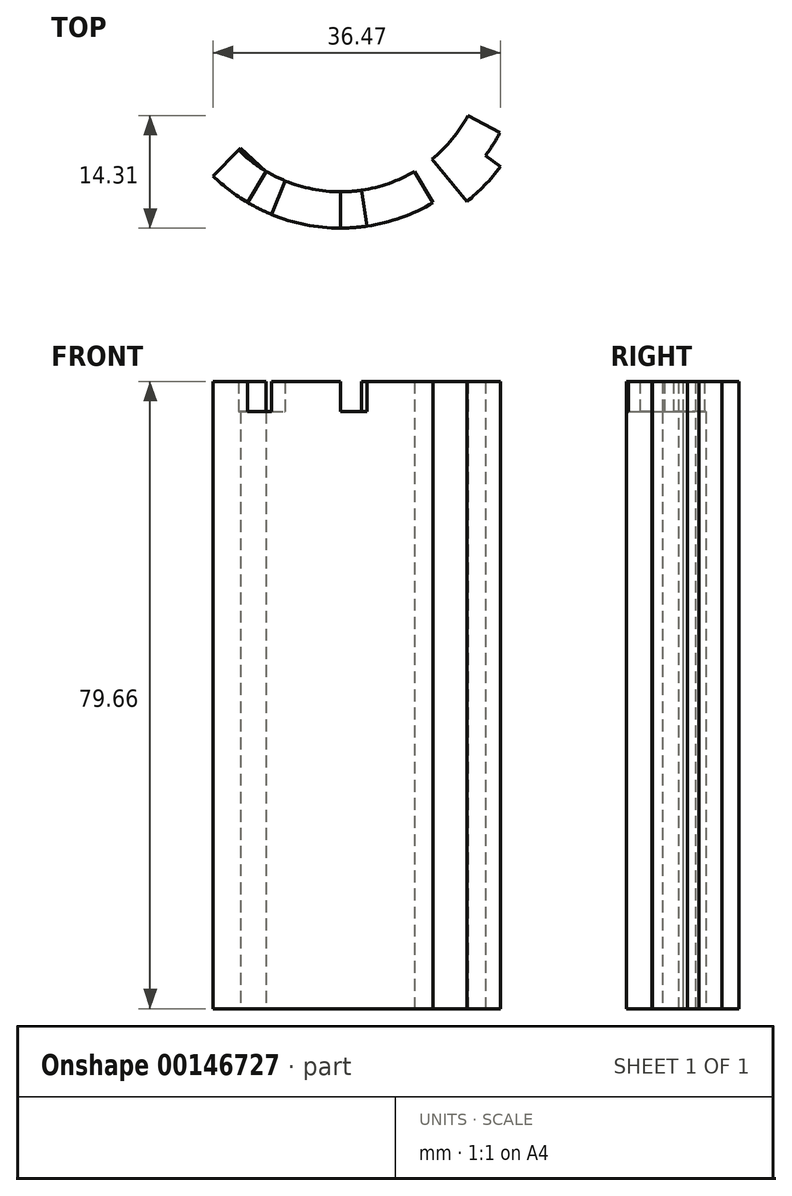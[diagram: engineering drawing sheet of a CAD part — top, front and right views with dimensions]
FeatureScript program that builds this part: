
annotation { "Feature Type Name" : "Feature", "Feature Type Description" : "" }
export const myFeature = defineFeature(function(context is Context, id is Id, definition is map)
    precondition{}
    {
        {
            var Q0;
            Q0=qCreatedBy(makeId("Top.planeOp"),FACE);
            var sketch = newSketch(context, id + "F0", { "sketchPlane" : qUnion([Q0])});
            skCircle(sketch, "E0", {"center": v(0, 0) * mm, "radius": 25.4 * mm});
            skLineSegment(sketch, "E1", {"start": v(-20.32, -15.24) * mm, "end": v(20.32, -15.24) * mm});
            skLineSegment(sketch, "E2", {"start": v(-20.32, -15.24) * mm, "end": v(0, 0) * mm});
            skLineSegment(sketch, "E3", {"start": v(20.32, -15.24) * mm, "end": v(0, 0) * mm});
            skCircle(sketch, "E4", {"center": v(0, 0) * mm, "radius": 18.41 * mm});
            skCircle(sketch, "E5", {"center": v(0, 0) * mm, "radius": 23.03 * mm});
            skCircle(sketch, "E6", {"center": v(0, 0) * mm, "radius": 16.14 * mm});
            skLineSegment(sketch, "E7", {"start": v(0, 0) * mm, "end": v(-17.81, -18.1) * mm});
            skLineSegment(sketch, "E8", {"start": v(-20.32, -15.24) * mm, "end": v(-17.81, -18.1) * mm});
            skLineSegment(sketch, "E9", {"start": v(-20.32, -15.24) * mm, "end": v(-23.38, -17.53) * mm});
            skLineSegment(sketch, "E10", {"start": v(-23.38, -17.53) * mm, "end": v(-20.5, -20.83) * mm});
            skLineSegment(sketch, "E11", {"start": v(-20.5, -20.83) * mm, "end": v(-17.81, -18.1) * mm});
            skLineSegment(sketch, "E12", {"start": v(-20.32, -15.24) * mm, "end": v(-8.94, 23.77) * mm});
            skLineSegment(sketch, "E13", {"start": v(-8.94, 23.77) * mm, "end": v(0, 0) * mm});
            skCircle(sketch, "E14", {"center": v(0, 0) * mm, "radius": 13.97 * mm});
            skLineSegment(sketch, "E15", {"start": v(0, 0) * mm, "end": v(22.37, -12.03) * mm});
            skLineSegment(sketch, "E16", {"start": v(0, 0) * mm, "end": v(-13.09, -21.98) * mm});
            skLineSegment(sketch, "E17", {"start": v(0, 0) * mm, "end": v(-9.66, -23.5) * mm});
            skLineSegment(sketch, "E18", {"start": v(0, 0) * mm, "end": v(0, -25.4) * mm});
            skLineSegment(sketch, "E19", {"start": v(0, 0) * mm, "end": v(3.72, -25.13) * mm});
            skLineSegment(sketch, "E20", {"start": v(0, 0) * mm, "end": v(13, -21.82) * mm});
            skLineSegment(sketch, "E21", {"start": v(0, 0) * mm, "end": v(16.05, -19.69) * mm});
            skLineSegment(sketch, "E22", {"start": v(-9.42, -15.82) * mm, "end": v(-7, -17.03) * mm});
            skLineSegment(sketch, "E23", {"start": v(0, -18.42) * mm, "end": v(2.7, -18.22) * mm});
            skLineSegment(sketch, "E24", {"start": v(9.42, -15.82) * mm, "end": v(11.64, -14.27) * mm});
            skLineSegment(sketch, "E25", {"start": v(-9.42, -15.82) * mm, "end": v(-14.73, -11.05) * mm});
            skLineSegment(sketch, "E26", {"start": v(-7, -17.03) * mm, "end": v(0, -18.41) * mm});
            skLineSegment(sketch, "E27", {"start": v(2.7, -18.22) * mm, "end": v(9.42, -15.82) * mm});
            skLineSegment(sketch, "E28", {"start": v(11.64, -14.27) * mm, "end": v(15.92, -8.56) * mm});
            skSolve(sketch);
        }
        {
            var Q0;
            {var subQ0=sQuery(id+"F0.wireOp",EDGE,"E5");var subQ1=sQuery(id+"F0.wireOp",EDGE,"E1");var subQ2=makeQuery(id+"F0.imprint","INTERSECT",VERTEX,{"disambiguationData":[OD(0.0)],"derivedFrom":[subQ1,subQ0]});Q0=makeQuery(id+"F0.imprint","IMPRINT",FACE,{"disambiguationData":[TD([[makeQuery(id+"F0.imprint","IMPRINT",EDGE,{"disambiguationData":[TD([[subQ2,-1.0]])],"derivedFrom":subQ1}),1.0]])]});}
            var Q1;
            {var subQ0=sQuery(id+"F0.wireOp",EDGE,"E5");var subQ1=sQuery(id+"F0.wireOp",EDGE,"E1");var subQ2=makeQuery(id+"F0.imprint","INTERSECT",VERTEX,{"disambiguationData":[OD(0.0)],"derivedFrom":[subQ1,subQ0]});Q1=makeQuery(id+"F0.imprint","IMPRINT",FACE,{"disambiguationData":[TD([[makeQuery(id+"F0.imprint","IMPRINT",EDGE,{"disambiguationData":[TD([[subQ2,-1.0]])],"derivedFrom":subQ1}),-1.0]])]});}
            var Q2;
            {var subQ0=sQuery(id+"F0.wireOp",EDGE,"E7");var subQ1=sQuery(id+"F0.wireOp",EDGE,"E1");var subQ2=makeQuery(id+"F0.imprint","INTERSECT",VERTEX,{"derivedFrom":[subQ1,subQ0]});Q2=makeQuery(id+"F0.imprint","IMPRINT",FACE,{"disambiguationData":[TD([[makeQuery(id+"F0.imprint","IMPRINT",EDGE,{"disambiguationData":[TD([[subQ2,-1.0]])],"derivedFrom":subQ1}),1.0]])]});}
            var Q3;
            {var subQ1=sQuery(id+"F0.wireOp",EDGE,"E1");var subQ6=sQuery(id+"F0.wireOp",EDGE,"E7");var subQ8=makeQuery(id+"F0.imprint","INTERSECT",VERTEX,{"derivedFrom":[subQ1,subQ6]});Q3=makeQuery(id+"F0.imprint","IMPRINT",FACE,{"disambiguationData":[TD([[makeQuery(id+"F0.imprint","IMPRINT",EDGE,{"disambiguationData":[TD([[subQ8,-1.0]])],"derivedFrom":subQ1}),-1.0]])]});}
            var Q4;
            {var subQ0=sQuery(id+"F0.wireOp",EDGE,"E4");var subQ1=sQuery(id+"F0.wireOp",EDGE,"E1");var subQ2=makeQuery(id+"F0.imprint","INTERSECT",VERTEX,{"disambiguationData":[OD(1.0)],"derivedFrom":[subQ1,subQ0]});Q4=makeQuery(id+"F0.imprint","IMPRINT",FACE,{"disambiguationData":[TD([[makeQuery(id+"F0.imprint","IMPRINT",EDGE,{"disambiguationData":[TD([[subQ2,-1.0]])],"derivedFrom":subQ1}),1.0]])]});}
            var Q5;
            {var subQ0=sQuery(id+"F0.wireOp",EDGE,"E5");var subQ1=sQuery(id+"F0.wireOp",EDGE,"E3");var subQ2=makeQuery(id+"F0.imprint","INTERSECT",VERTEX,{"derivedFrom":[subQ1,subQ0]});Q5=makeQuery(id+"F0.imprint","IMPRINT",FACE,{"disambiguationData":[TD([[makeQuery(id+"F0.imprint","IMPRINT",EDGE,{"disambiguationData":[TD([[subQ2,-1.0]])],"derivedFrom":subQ1}),-1.0]])]});}
            var Q6;
            {var subQ1=sQuery(id+"F0.wireOp",EDGE,"E1");var subQ5=sQuery(id+"F0.wireOp",EDGE,"E21");var subQ9=makeQuery(id+"F0.imprint","INTERSECT",VERTEX,{"derivedFrom":[subQ1,subQ5]});Q6=makeQuery(id+"F0.imprint","IMPRINT",FACE,{"disambiguationData":[TD([[makeQuery(id+"F0.imprint","IMPRINT",EDGE,{"disambiguationData":[TD([[subQ9,-1.0]])],"derivedFrom":subQ1}),1.0]])]});}
            var Q7;
            {var subQ0=sQuery(id+"F0.wireOp",EDGE,"E21");var subQ1=sQuery(id+"F0.wireOp",EDGE,"E1");var subQ2=makeQuery(id+"F0.imprint","INTERSECT",VERTEX,{"derivedFrom":[subQ1,subQ0]});Q7=makeQuery(id+"F0.imprint","IMPRINT",FACE,{"disambiguationData":[TD([[makeQuery(id+"F0.imprint","IMPRINT",EDGE,{"disambiguationData":[TD([[subQ2,-1.0]])],"derivedFrom":subQ1}),-1.0]])]});}
            var Q8;
            {var subQ1=sQuery(id+"F0.wireOp",EDGE,"E4");var subQ6=sQuery(id+"F0.wireOp",EDGE,"E1");var subQ9=makeQuery(id+"F0.imprint","INTERSECT",VERTEX,{"disambiguationData":[OD(1.0)],"derivedFrom":[subQ6,subQ1]});Q8=makeQuery(id+"F0.imprint","IMPRINT",FACE,{"disambiguationData":[TD([[makeQuery(id+"F0.imprint","IMPRINT",EDGE,{"disambiguationData":[TD([[subQ9,-1.0]])],"derivedFrom":subQ6}),-1.0]])]});}
            var Q9;
            {var subQ1=sQuery(id+"F0.wireOp",EDGE,"E19");var subQ6=sQuery(id+"F0.wireOp",EDGE,"E5");var subQ7=makeQuery(id+"F0.imprint","INTERSECT",VERTEX,{"derivedFrom":[subQ6,subQ1]});Q9=makeQuery(id+"F0.imprint","IMPRINT",FACE,{"disambiguationData":[TD([[makeQuery(id+"F0.imprint","IMPRINT",EDGE,{"disambiguationData":[TD([[subQ7,-1.0]])],"derivedFrom":subQ6}),1.0]])]});}
            var Q10;
            {var subQ1=sQuery(id+"F0.wireOp",EDGE,"E16");var subQ6=sQuery(id+"F0.wireOp",EDGE,"E5");var subQ7=makeQuery(id+"F0.imprint","INTERSECT",VERTEX,{"derivedFrom":[subQ6,subQ1]});Q10=makeQuery(id+"F0.imprint","IMPRINT",FACE,{"disambiguationData":[TD([[makeQuery(id+"F0.imprint","IMPRINT",EDGE,{"disambiguationData":[TD([[subQ7,-1.0]])],"derivedFrom":subQ6}),1.0]])]});}
            var Q11;
            {var subQ1=sQuery(id+"F0.wireOp",EDGE,"E17");var subQ6=sQuery(id+"F0.wireOp",EDGE,"E5");var subQ7=makeQuery(id+"F0.imprint","INTERSECT",VERTEX,{"derivedFrom":[subQ6,subQ1]});Q11=makeQuery(id+"F0.imprint","IMPRINT",FACE,{"disambiguationData":[TD([[makeQuery(id+"F0.imprint","IMPRINT",EDGE,{"disambiguationData":[TD([[subQ7,-1.0]])],"derivedFrom":subQ6}),1.0]])]});}
            var Q12;
            {var subQ1=sQuery(id+"F0.wireOp",EDGE,"E18");var subQ6=sQuery(id+"F0.wireOp",EDGE,"E5");var subQ7=makeQuery(id+"F0.imprint","INTERSECT",VERTEX,{"derivedFrom":[subQ6,subQ1]});Q12=makeQuery(id+"F0.imprint","IMPRINT",FACE,{"disambiguationData":[TD([[makeQuery(id+"F0.imprint","IMPRINT",EDGE,{"disambiguationData":[TD([[subQ7,-1.0]])],"derivedFrom":subQ6}),1.0]])]});}
            extrude(context, id + "F1", {"entities" : qUnion([Q0, Q1, Q2, Q3, Q4, Q5, Q6, Q7, Q8, Q9, Q10, Q11, Q12]), "depth" : 36.02 * mm, "hasSecondDirection" : true, "secondDirectionOppositeDirection" : true, "secondDirectionDepth" : 39.83 * mm});
        }
        {
            var Q0;
            {var subQ0=sQuery(id+"F0.wireOp",EDGE,"E5");var subQ1=sQuery(id+"F0.wireOp",EDGE,"E1");var subQ2=makeQuery(id+"F0.imprint","INTERSECT",VERTEX,{"disambiguationData":[OD(0.0)],"derivedFrom":[subQ1,subQ0]});Q0=makeQuery(id+"F0.imprint","IMPRINT",FACE,{"disambiguationData":[TD([[makeQuery(id+"F0.imprint","IMPRINT",EDGE,{"disambiguationData":[TD([[subQ2,-1.0]])],"derivedFrom":subQ1}),1.0]])]});}
            var Q1;
            {var subQ0=sQuery(id+"F0.wireOp",EDGE,"E5");var subQ1=sQuery(id+"F0.wireOp",EDGE,"E1");var subQ2=makeQuery(id+"F0.imprint","INTERSECT",VERTEX,{"disambiguationData":[OD(0.0)],"derivedFrom":[subQ1,subQ0]});Q1=makeQuery(id+"F0.imprint","IMPRINT",FACE,{"disambiguationData":[TD([[makeQuery(id+"F0.imprint","IMPRINT",EDGE,{"disambiguationData":[TD([[subQ2,-1.0]])],"derivedFrom":subQ1}),-1.0]])]});}
            var Q2;
            {var subQ0=sQuery(id+"F0.wireOp",EDGE,"E7");var subQ1=sQuery(id+"F0.wireOp",EDGE,"E1");var subQ2=makeQuery(id+"F0.imprint","INTERSECT",VERTEX,{"derivedFrom":[subQ1,subQ0]});Q2=makeQuery(id+"F0.imprint","IMPRINT",FACE,{"disambiguationData":[TD([[makeQuery(id+"F0.imprint","IMPRINT",EDGE,{"disambiguationData":[TD([[subQ2,-1.0]])],"derivedFrom":subQ1}),1.0]])]});}
            var Q3;
            {var subQ0=sQuery(id+"F0.wireOp",EDGE,"E7");var subQ1=sQuery(id+"F0.wireOp",EDGE,"E1");var subQ2=makeQuery(id+"F0.imprint","INTERSECT",VERTEX,{"derivedFrom":[subQ1,subQ0]});Q3=makeQuery(id+"F0.imprint","IMPRINT",FACE,{"disambiguationData":[TD([[makeQuery(id+"F0.imprint","IMPRINT",EDGE,{"disambiguationData":[TD([[subQ2,-1.0]])],"derivedFrom":subQ1}),-1.0]])]});}
            var Q4;
            {var subQ1=sQuery(id+"F0.wireOp",EDGE,"E17");var subQ6=sQuery(id+"F0.wireOp",EDGE,"E5");var subQ7=makeQuery(id+"F0.imprint","INTERSECT",VERTEX,{"derivedFrom":[subQ6,subQ1]});Q4=makeQuery(id+"F0.imprint","IMPRINT",FACE,{"disambiguationData":[TD([[makeQuery(id+"F0.imprint","IMPRINT",EDGE,{"disambiguationData":[TD([[subQ7,-1.0]])],"derivedFrom":subQ6}),1.0]])]});}
            var Q5;
            {var subQ1=sQuery(id+"F0.wireOp",EDGE,"E19");var subQ6=sQuery(id+"F0.wireOp",EDGE,"E5");var subQ7=makeQuery(id+"F0.imprint","INTERSECT",VERTEX,{"derivedFrom":[subQ6,subQ1]});Q5=makeQuery(id+"F0.imprint","IMPRINT",FACE,{"disambiguationData":[TD([[makeQuery(id+"F0.imprint","IMPRINT",EDGE,{"disambiguationData":[TD([[subQ7,-1.0]])],"derivedFrom":subQ6}),1.0]])]});}
            var Q6;
            {var subQ0=sQuery(id+"F0.wireOp",EDGE,"E21");var subQ1=sQuery(id+"F0.wireOp",EDGE,"E1");var subQ2=makeQuery(id+"F0.imprint","INTERSECT",VERTEX,{"derivedFrom":[subQ1,subQ0]});Q6=makeQuery(id+"F0.imprint","IMPRINT",FACE,{"disambiguationData":[TD([[makeQuery(id+"F0.imprint","IMPRINT",EDGE,{"disambiguationData":[TD([[subQ2,-1.0]])],"derivedFrom":subQ1}),-1.0]])]});}
            var Q7;
            {var subQ1=sQuery(id+"F0.wireOp",EDGE,"E1");var subQ5=sQuery(id+"F0.wireOp",EDGE,"E21");var subQ9=makeQuery(id+"F0.imprint","INTERSECT",VERTEX,{"derivedFrom":[subQ1,subQ5]});Q7=makeQuery(id+"F0.imprint","IMPRINT",FACE,{"disambiguationData":[TD([[makeQuery(id+"F0.imprint","IMPRINT",EDGE,{"disambiguationData":[TD([[subQ9,-1.0]])],"derivedFrom":subQ1}),1.0]])]});}
            var Q8;
            {var subQ0=sQuery(id+"F0.wireOp",EDGE,"E5");var subQ1=sQuery(id+"F0.wireOp",EDGE,"E3");var subQ2=makeQuery(id+"F0.imprint","INTERSECT",VERTEX,{"derivedFrom":[subQ1,subQ0]});Q8=makeQuery(id+"F0.imprint","IMPRINT",FACE,{"disambiguationData":[TD([[makeQuery(id+"F0.imprint","IMPRINT",EDGE,{"disambiguationData":[TD([[subQ2,-1.0]])],"derivedFrom":subQ1}),-1.0]])]});}
            extrude(context, id + "F2", {"entities" : qUnion([Q0, Q1, Q2, Q3, Q4, Q5, Q6, Q7, Q8]), "operationType" : NewBodyOperationType.ADD, "depth" : 39.83 * mm});
        }
    });
